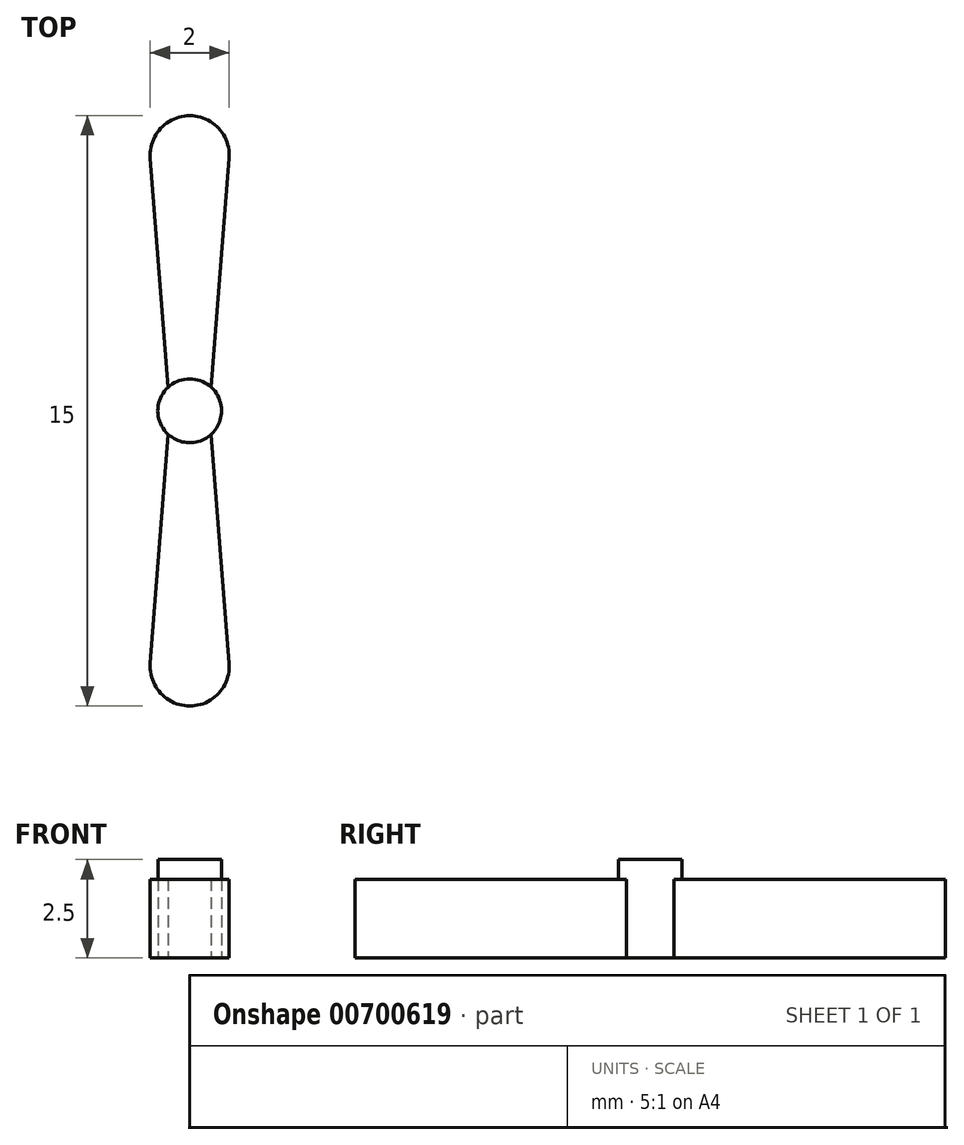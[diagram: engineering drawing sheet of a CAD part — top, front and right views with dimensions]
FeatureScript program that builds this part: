
annotation { "Feature Type Name" : "Feature", "Feature Type Description" : "" }
export const myFeature = defineFeature(function(context is Context, id is Id, definition is map)
    precondition{}
    {
        {
            var Q0;
            Q0=qCreatedBy(makeId("Top.planeOp"),FACE);
            var sketch = newSketch(context, id + "F0", { "sketchPlane" : qUnion([Q0])});
            skLineSegment(sketch, "E0", {"start": v(-2.34, 0) * mm, "end": v(-1.34, 0) * mm, "construction": true});
            skLineSegment(sketch, "E1", {"start": v(-1.84, 0) * mm, "end": v(-1.84, 6.47) * mm, "construction": true});
            skLineSegment(sketch, "E2", {"start": v(-2.34, 0) * mm, "end": v(-2.84, 6.42) * mm});
            skLineSegment(sketch, "E3.MirrorCS", {"start": v(-1.34, 0) * mm, "end": v(-0.84, 6.42) * mm});
            skArc(sketch, "E4", {"start": v(-0.84, 6.42) * mm, "mid": v(-1.84, 7.5) * mm, "end": v(-2.84, 6.42) * mm});
            skLineSegment(sketch, "E5.MirrorCS", {"start": v(-1.34, 0) * mm, "end": v(-0.84, -6.42) * mm});
            skLineSegment(sketch, "E6.MirrorCS", {"start": v(-2.34, 0) * mm, "end": v(-2.84, -6.42) * mm});
            skArc(sketch, "E7.MirrorCS", {"start": v(-0.84, -6.42) * mm, "mid": v(-1.84, -7.5) * mm, "end": v(-2.84, -6.42) * mm});
            skSolve(sketch);
        }
        {
            var Q0;
            Q0 = qSketchRegion(id + "F0", true);
            extrude(context, id + "F1", {"entities" : qUnion([Q0]), "depth" : 2 * mm, "offsetDistance" : 25.4 * mm});
        }
        {
            var Q0;
            Q0=makeQuery(id+"F1.opExtrude","CAP_FACE",FACE,{"disambiguationData":[OSD([sQuery(id+"F0.wireOp",EDGE,"E2"),sQuery(id+"F0.wireOp",EDGE,"E3.MirrorCS"),sQuery(id+"F0.wireOp",EDGE,"E4"),sQuery(id+"F0.wireOp",EDGE,"E5.MirrorCS"),sQuery(id+"F0.wireOp",EDGE,"E6.MirrorCS"),sQuery(id+"F0.wireOp",EDGE,"E7.MirrorCS")])],"isStart":false});
            var sketch = newSketch(context, id + "F2", { "sketchPlane" : qUnion([Q0])});
            skLineSegment(sketch, "E8", {"start": v(-2.34, 0) * mm, "end": v(-1.34, 0) * mm, "construction": true});
            skCircle(sketch, "E9", {"center": v(-1.84, 0) * mm, "radius": 0.8 * mm});
            skSolve(sketch);
        }
        {
            var Q0;
            Q0 = qSketchRegion(id + "F2", true);
            extrude(context, id + "F3", {"entities" : qUnion([Q0]), "operationType" : NewBodyOperationType.ADD, "depth" : .5 * mm, "offsetDistance" : 25.4 * mm, "hasSecondDirection" : true, "secondDirectionOppositeDirection" : true, "secondDirectionDepth" : 2 * mm});
        }
    });
